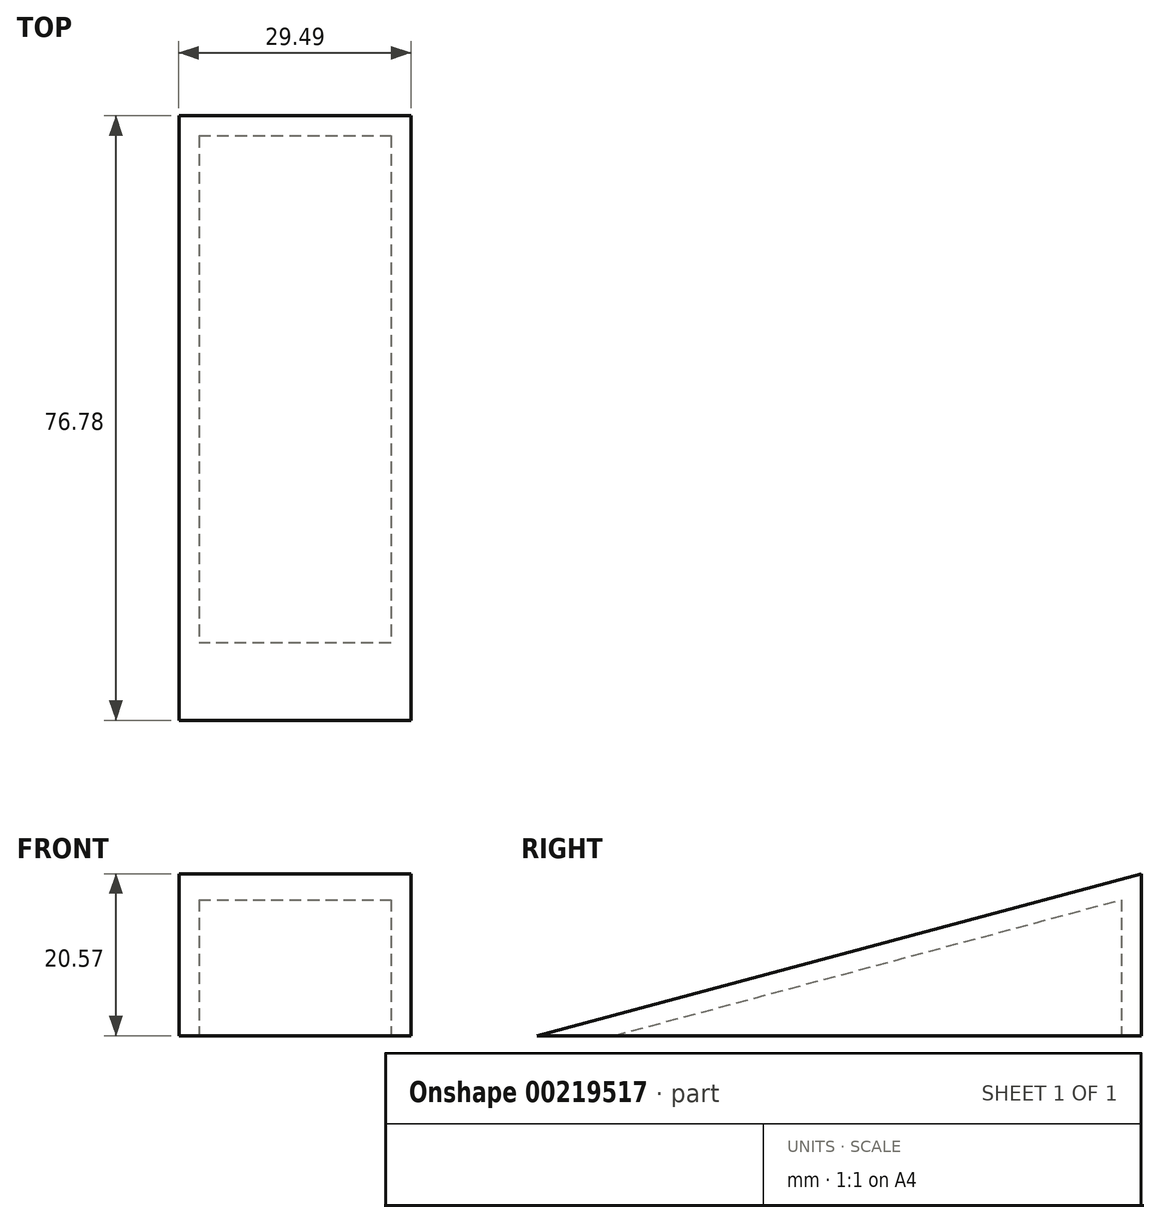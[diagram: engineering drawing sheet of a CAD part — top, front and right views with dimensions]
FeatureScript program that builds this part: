
annotation { "Feature Type Name" : "Feature", "Feature Type Description" : "" }
export const myFeature = defineFeature(function(context is Context, id is Id, definition is map)
    precondition{}
    {
        {
            var Q0;
            Q0=qCreatedBy(makeId("Top.planeOp"),FACE);
            var sketch = newSketch(context, id + "F0", { "sketchPlane" : qUnion([Q0])});
            skLineSegment(sketch, "E0.bottom", {"start": v(-30.35, 45.82) * mm, "end": v(-0.86, 45.82) * mm});
            skLineSegment(sketch, "E0.top", {"start": v(-30.35, -33.86) * mm, "end": v(-0.86, -33.86) * mm});
            skLineSegment(sketch, "E0.left", {"start": v(-30.35, 45.82) * mm, "end": v(-30.35, -33.86) * mm});
            skLineSegment(sketch, "E0.right", {"start": v(-0.86, 45.82) * mm, "end": v(-0.86, -33.86) * mm});
            skSolve(sketch);
        }
        {
            var Q0;
            Q0=makeQuery(id+"F0.imprint","IMPRINT",FACE,{"disambiguationData":[TD([[makeQuery(id+"F0.imprint","IMPRINT",EDGE,{"derivedFrom":sQuery(id+"F0.wireOp",EDGE,"E0.bottom")}),-1.0]])]});
            extrude(context, id + "F1", {"entities" : qUnion([Q0]), "depth" : 20.57 * mm});
        }
        {
            var Q0;
            Q0=makeQuery(id+"F1.opExtrude","CAP_EDGE",EDGE,{"disambiguationData":[OSD([sQuery(id+"F0.wireOp",EDGE,"E0.top")])],"isStart":false});
            chamfer(context, id + "F2", {"entities" : qUnion([Q0]), "chamferType" : ChamferType.OFFSET_ANGLE, "width" : 79.68 * mm, "oppositeDirection" : false, "angle" : 15 * degree, "tangentPropagation" : true});
        }
        {
            var Q0;
            Q0=makeQuery(id+"F1.opExtrude","CAP_FACE",FACE,{"disambiguationData":[OSD([sQuery(id+"F0.wireOp",EDGE,"E0.bottom"),sQuery(id+"F0.wireOp",EDGE,"E0.top"),sQuery(id+"F0.wireOp",EDGE,"E0.left"),sQuery(id+"F0.wireOp",EDGE,"E0.right")])],"isStart":true});
            shell(context, id + "F3", {"entities" : qUnion([Q0]), "thickness" : 2.54 * mm});
        }
    });
